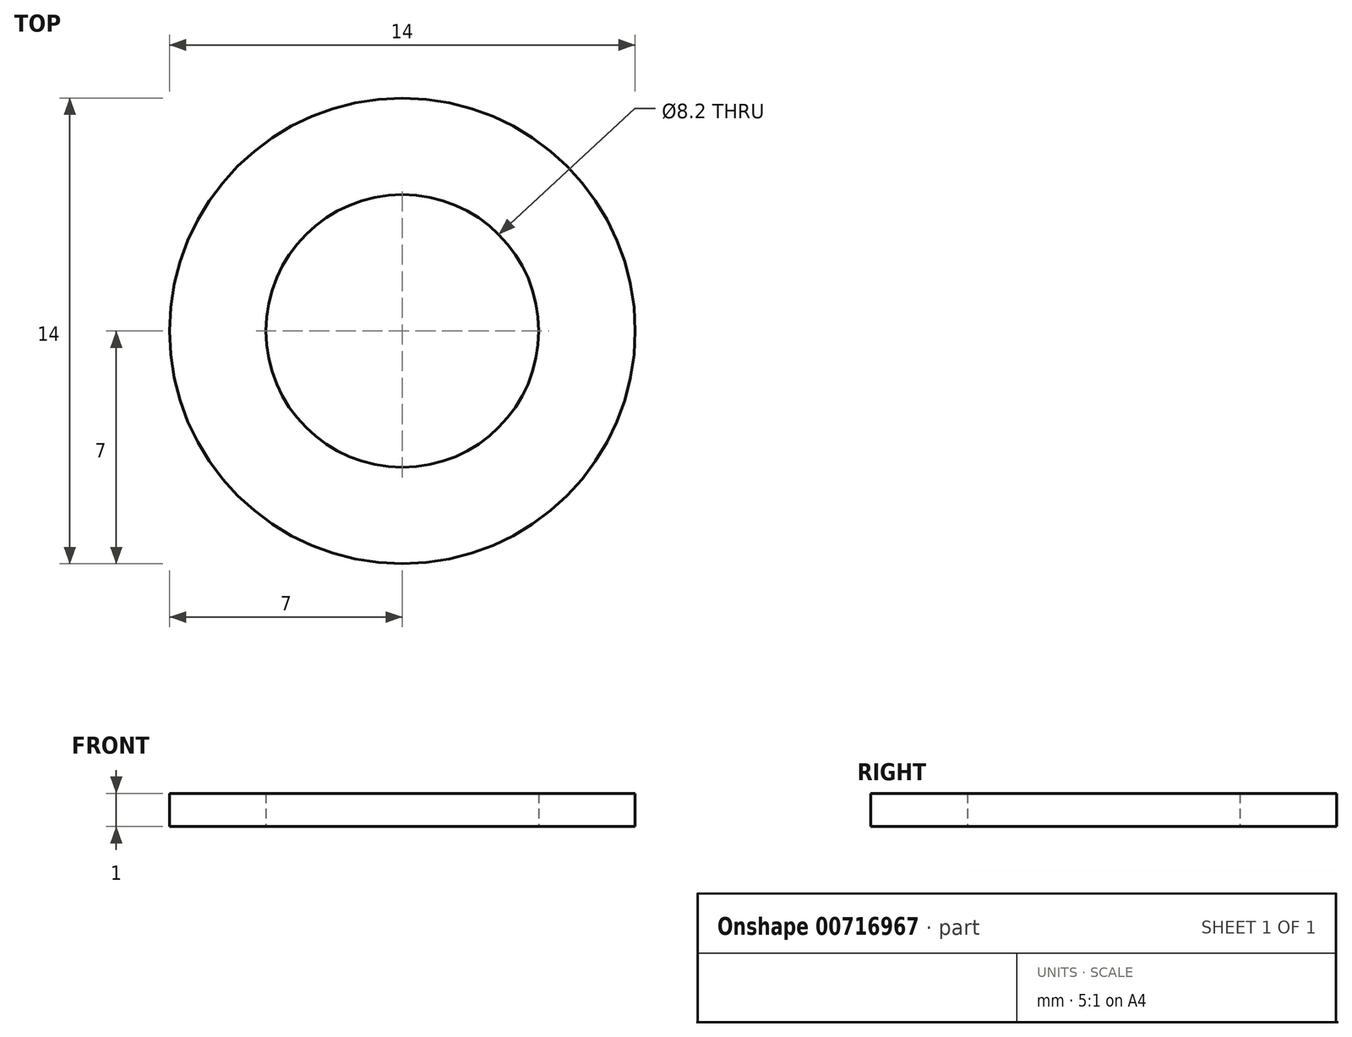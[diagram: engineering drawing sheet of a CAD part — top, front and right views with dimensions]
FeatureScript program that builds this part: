
annotation { "Feature Type Name" : "Feature", "Feature Type Description" : "" }
export const myFeature = defineFeature(function(context is Context, id is Id, definition is map)
    precondition{}
    {
        {
            var Q0;
            Q0=qCreatedBy(makeId("Top.planeOp"),FACE);
            var sketch = newSketch(context, id + "F0", { "sketchPlane" : qUnion([Q0])});
            skCircle(sketch, "E0", {"center": v(0, 0) * mm, "radius": 4.1 * mm});
            skCircle(sketch, "E1", {"center": v(0, 0) * mm, "radius": 7 * mm});
            skSolve(sketch);
        }
        {
            var Q0;
            Q0=makeQuery(id+"F0.imprint","IMPRINT",FACE,{"disambiguationData":[TD([[makeQuery(id+"F0.imprint","IMPRINT",EDGE,{"derivedFrom":sQuery(id+"F0.wireOp",EDGE,"E0")}),-1.0]])]});
            extrude(context, id + "F1", {"entities" : qUnion([Q0]), "depth" : 1 * mm, "offsetDistance" : 25 * mm});
        }
    });
